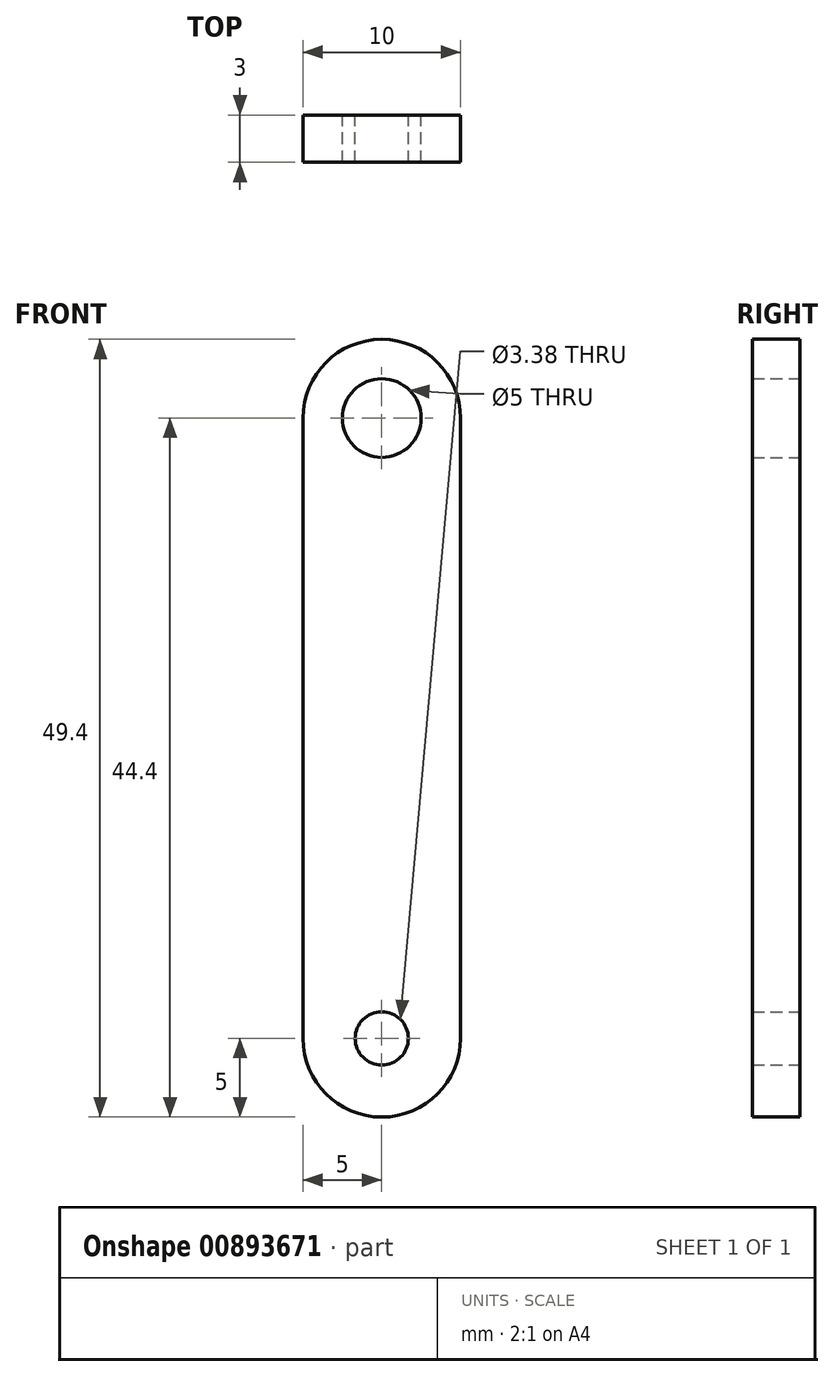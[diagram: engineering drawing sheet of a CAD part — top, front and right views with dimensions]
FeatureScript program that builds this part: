
annotation { "Feature Type Name" : "Feature", "Feature Type Description" : "" }
export const myFeature = defineFeature(function(context is Context, id is Id, definition is map)
    precondition{}
    {
        {
            var Q0;
            Q0=qCreatedBy(makeId("Front.planeOp"),FACE);
            var sketch = newSketch(context, id + "F0", { "sketchPlane" : qUnion([Q0])});
            skLineSegment(sketch, "E0.left", {"start": v(5, -19.7) * mm, "end": v(5, 19.7) * mm});
            skLineSegment(sketch, "E0.right", {"start": v(-5, -19.7) * mm, "end": v(-5, 19.7) * mm});
            skPoint(sketch, "E0.middle", {"position": v(0, 0) * mm});
            skArc(sketch, "E1", {"start": v(5, 19.7) * mm, "mid": v(0, 24.7) * mm, "end": v(-5, 19.7) * mm});
            skArc(sketch, "E2", {"start": v(-5, -19.7) * mm, "mid": v(0, -24.7) * mm, "end": v(5, -19.7) * mm});
            skCircle(sketch, "E3", {"center": v(0, -19.7) * mm, "radius": 1.69 * mm});
            skCircle(sketch, "E4", {"center": v(0, 19.7) * mm, "radius": 2.5 * mm});
            skSolve(sketch);
        }
        {
            var Q0;
            Q0 = qSketchRegion(id + "F0", true);
            extrude(context, id + "F1", {"entities" : qUnion([Q0]), "depth" : 3 * mm, "offsetDistance" : 25 * mm});
        }
    });
